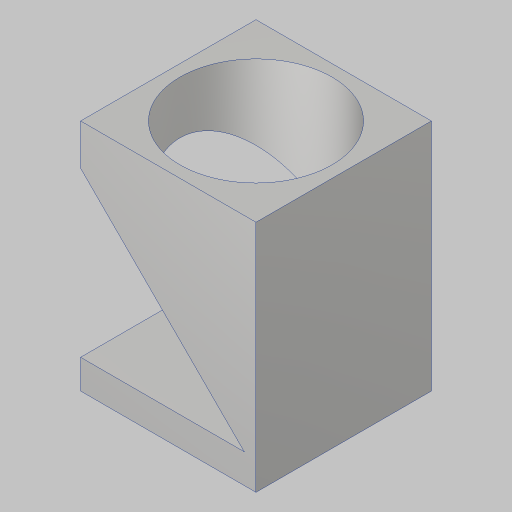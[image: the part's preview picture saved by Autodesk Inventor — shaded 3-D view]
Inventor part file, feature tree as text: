
AUTODESK INVENTOR PART (.ipt)
format: ipt  version: 2023.5 (Build 275446000, 446)  size: 121,344 bytes
history: native  units: in
note: dims shown in document units (in); Inventor stores cm internally (conversion verified against a paired STEP export)
features: extrude x3, sketch x3, projected_geometry x3
ambient origin geometry x8: Origin, YZ Plane, XZ Plane, XY Plane, X Axis, Y Axis, Z Axis, Center Point
bodies: Solid1 (feature_tree)
feature tree (9):
  extrude  "Extrusion1"  Depth=3.0in
  extrude  "Extrusion2"  Depth=4.0in
  extrude  "Extrusion3"  TaperAngle=45.0deg  [1 undecoded]
  sketch  "Sketch1"  dims[d0=3.0in d1=3.0in]
  sketch  "Sketch2"  dims[d2=4.0in d3=0.0in d4=2.6in]
  sketch  "Sketch3"  dims[d5=3.5in d6=0.0in d7=45.0deg d8=0.0in d9=0.0in]
  projected_geometry  "Projected Loop1"
  projected_geometry  "Project Cut Edges1"
  projected_geometry  "Project Cut Edges2"
note: 1 required parameter value undecoded (feature->parameter linkage not recoverable at this tier; creation-order binding heuristic only, values carry confidence <= 0.55)
